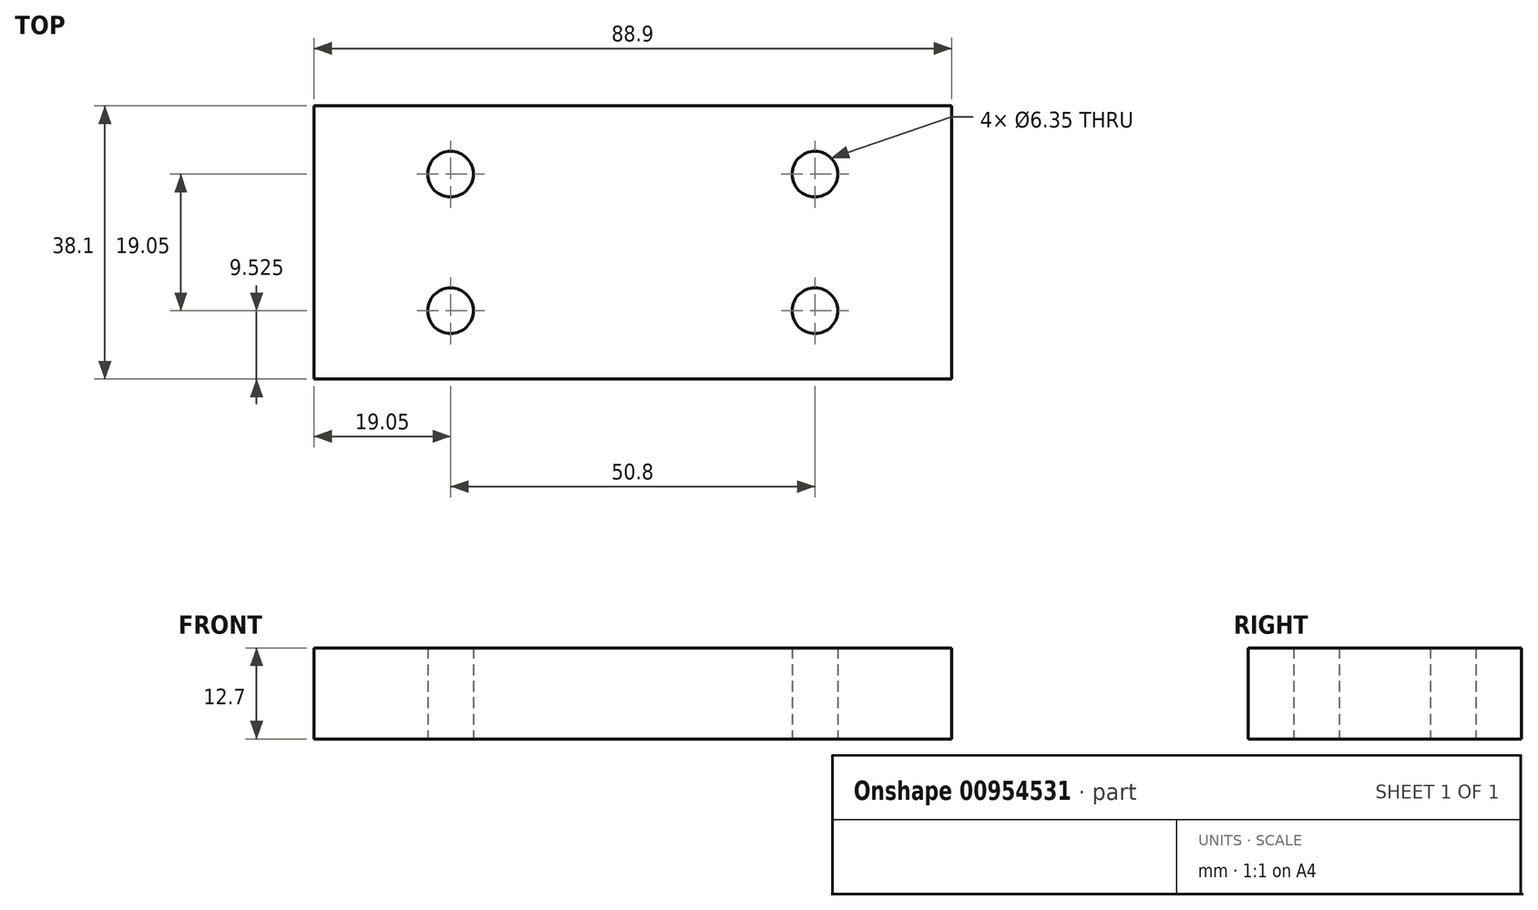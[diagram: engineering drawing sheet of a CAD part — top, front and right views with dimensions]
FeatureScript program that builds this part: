
annotation { "Feature Type Name" : "Feature", "Feature Type Description" : "" }
export const myFeature = defineFeature(function(context is Context, id is Id, definition is map)
    precondition{}
    {
        {
            var Q0;
            Q0=qCreatedBy(makeId("Top.planeOp"),FACE);
            var sketch = newSketch(context, id + "F0", { "sketchPlane" : qUnion([Q0])});
            skLineSegment(sketch, "E0.bottom", {"start": v(44.45, -19.05) * mm, "end": v(-44.45, -19.05) * mm});
            skLineSegment(sketch, "E0.top", {"start": v(44.45, 19.05) * mm, "end": v(-44.45, 19.05) * mm});
            skLineSegment(sketch, "E0.left", {"start": v(44.45, -19.05) * mm, "end": v(44.45, 19.05) * mm});
            skLineSegment(sketch, "E0.right", {"start": v(-44.45, -19.05) * mm, "end": v(-44.45, 19.05) * mm});
            skPoint(sketch, "E0.middle", {"position": v(0, 0) * mm});
            skLineSegment(sketch, "E1.bottom", {"start": v(25.4, -9.53) * mm, "end": v(-25.4, -9.53) * mm, "construction": true});
            skLineSegment(sketch, "E1.top", {"start": v(25.4, 9.53) * mm, "end": v(-25.4, 9.52) * mm, "construction": true});
            skLineSegment(sketch, "E1.left", {"start": v(25.4, -9.53) * mm, "end": v(25.4, 9.53) * mm, "construction": true});
            skLineSegment(sketch, "E1.right", {"start": v(-25.4, -9.53) * mm, "end": v(-25.4, 9.53) * mm, "construction": true});
            skCircle(sketch, "E2", {"center": v(-25.4, 9.53) * mm, "radius": 3.18 * mm});
            skCircle(sketch, "E3", {"center": v(25.4, 9.53) * mm, "radius": 3.18 * mm});
            skCircle(sketch, "E4", {"center": v(-25.4, -9.53) * mm, "radius": 3.18 * mm});
            skCircle(sketch, "E5", {"center": v(25.4, -9.53) * mm, "radius": 3.18 * mm});
            skSolve(sketch);
        }
        {
            var Q0;
            Q0 = qSketchRegion(id + "F0", true);
            extrude(context, id + "F1", {"entities" : qUnion([Q0]), "depth" : 12.7 * mm, "offsetDistance" : 25.4 * mm});
        }
    });
